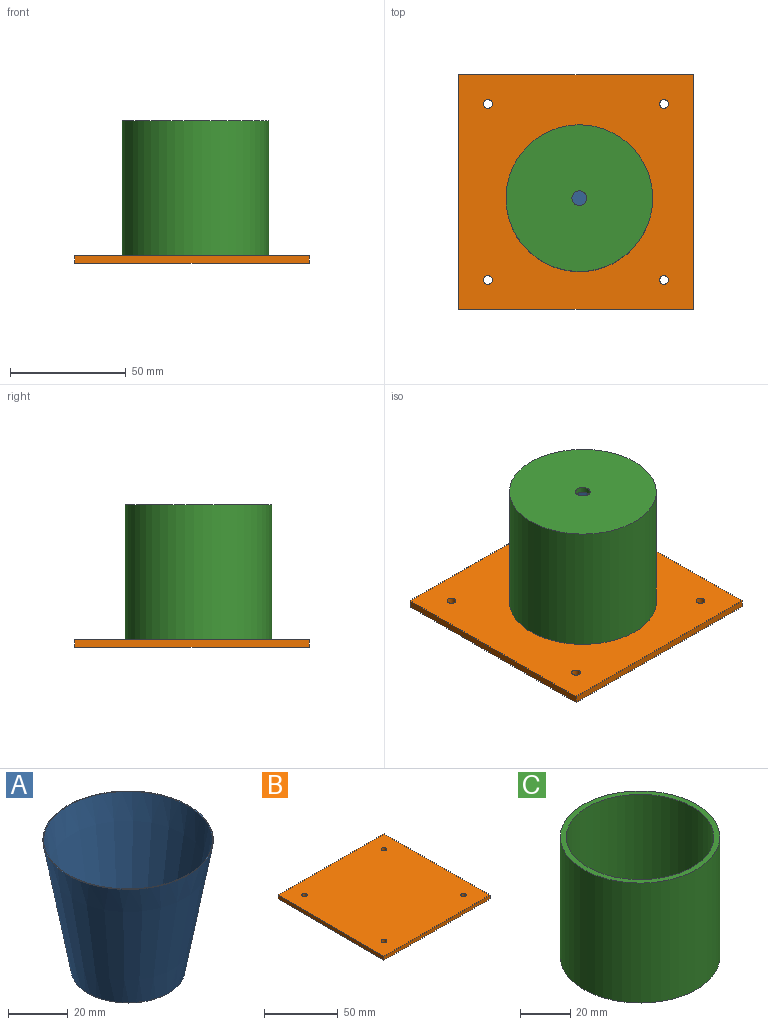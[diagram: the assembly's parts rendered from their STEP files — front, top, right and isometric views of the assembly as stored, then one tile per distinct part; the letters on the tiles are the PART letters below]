
ASSEMBLY  parts=3 mates=3
PART A: 5 faces, bbox 57.2x57.2x53.3 mm
  f0: plane 57.15x57.15mm, normal (0,0,1), area 46.1mm2, adj f2,f4
  f1: plane 38.1x38.1mm, normal (0,0,-1), area 1140.1mm2, adj f2
  f2: cone r=28.57mm half-angle=10.1deg, axis (0,0,1), area 8106.9mm2, adj f0,f1
  f3: plane 37.67x37.67mm, normal (0,0,1), area 1114.8mm2, adj f4
  f4: cone r=28.32mm half-angle=10.1deg, axis (0,0,1), area 7988.5mm2, adj f0,f3
PART B: 10 faces, bbox 101.6x101.6x3.2 mm
  f0: plane 101.6x3.18mm, normal (-1,0,0), area 322.6mm2, adj f1,f7,f8,f9
  f1: plane 101.6x3.18mm, normal (0,1,0), area 322.6mm2, adj f0,f2,f8,f9
  f2: plane 101.6x3.18mm, normal (1,0,0), area 322.6mm2, adj f1,f7,f8,f9
  f3: cylinder r=1.91mm len=3.81mm, axis (0,0,1), area 38mm2, adj f8,f9
  f4: cylinder r=1.91mm len=3.81mm, axis (0,0,1), area 38mm2, adj f8,f9
  f5: cylinder r=1.91mm len=3.81mm, axis (0,0,1), area 38mm2, adj f8,f9
  f6: cylinder r=1.91mm len=3.81mm, axis (0,0,1), area 38mm2, adj f8,f9
  f7: plane 101.6x3.18mm, normal (0,-1,0), area 322.6mm2, adj f0,f2,f8,f9
  f8: plane 101.6x101.6mm, normal (0,0,-1), area 10277mm2, adj f0,f1,f2,f3,f4,f5,f6,f7
  f9: plane 101.6x101.6mm, normal (0,0,1), area 10277mm2, adj f0,f1,f2,f3,f4,f5,f6,f7
PART C: 6 faces, bbox 63.5x63.5x58.4 mm
  f0: cylinder r=29.37mm len=58.74mm, axis (0,0,-1), area 10311.5mm2, adj f2,f4
  f1: cylinder r=31.75mm len=63.5mm, axis (0,0,-1), area 11654.3mm2, adj f2,f3
  f2: plane 63.5x63.5mm, normal (0,0,1), area 457.2mm2, adj f0,f1
  f3: plane 63.5x63.5mm, normal (0,0,-1), area 3135.3mm2, adj f1,f5
  f4: plane 58.74x58.74mm, normal (0,0,1), area 2678mm2, adj f0,f5
  f5: cylinder r=3.17mm len=6.35mm, axis (0,0,-1), area 50.7mm2, adj f3,f4
PLACE A t=(-11.31,-124.91,-352.78)mm
PLACE B t=(-12.74,-122.14,-352.78)mm
PLACE C rot(axis=(1,0,0),180deg) t=(-11.31,-124.91,-294.36)mm
MATE planar C.f0 <-> B.f9  axis (0,0,-1) through (-11.31,-124.91,-352.78)mm
MATE planar A.f2 <-> B.f9  axis (0,0,-1) through (-11.31,-124.91,-352.78)mm
MATE cylindrical C.f0 <-> A.f2  axis (0,0,1) through (-11.31,-124.91,-294.36)mm
